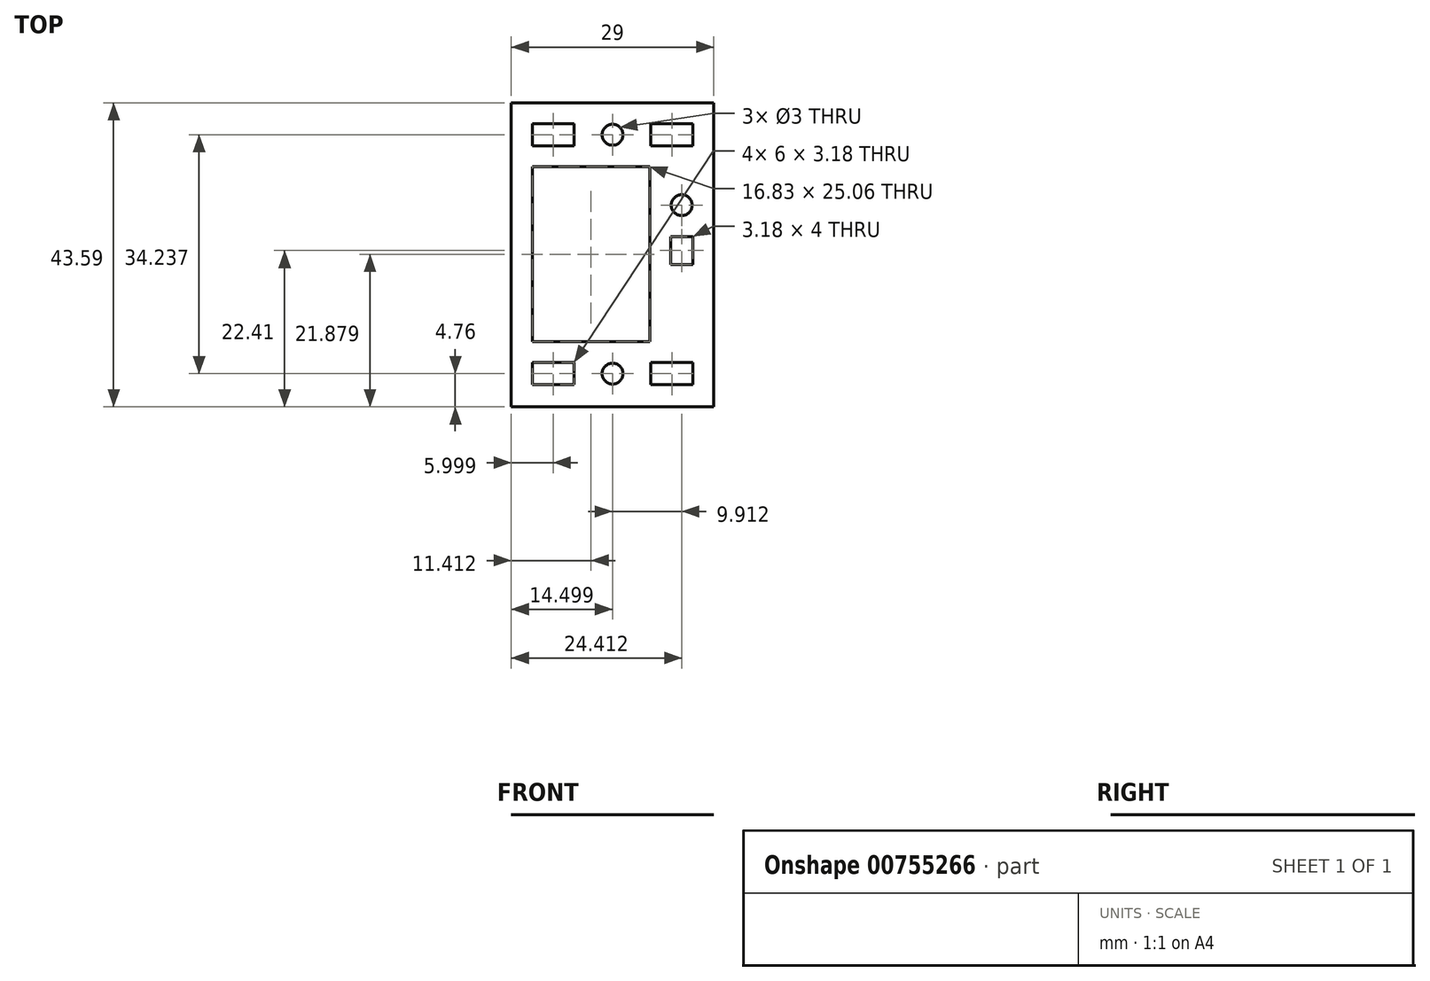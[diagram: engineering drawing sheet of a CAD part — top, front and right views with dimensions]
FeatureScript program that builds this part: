
annotation { "Feature Type Name" : "Feature", "Feature Type Description" : "" }
export const myFeature = defineFeature(function(context is Context, id is Id, definition is map)
    precondition{}
    {
        {
            var Q0;
            Q0=qCreatedBy(makeId("Top.planeOp"),FACE);
            var sketch = newSketch(context, id + "F0", { "sketchPlane" : qUnion([Q0])});
            skCircle(sketch, "E0", {"center": v(-29.12, -7.63) * mm, "radius": 1.5 * mm});
            skLineSegment(sketch, "E1.bottom", {"start": v(-23.62, -6.04) * mm, "end": v(-17.62, -6.04) * mm});
            skLineSegment(sketch, "E1.top", {"start": v(-23.62, -9.22) * mm, "end": v(-17.62, -9.22) * mm});
            skLineSegment(sketch, "E1.left", {"start": v(-23.62, -6.04) * mm, "end": v(-23.62, -9.22) * mm});
            skLineSegment(sketch, "E1.right", {"start": v(-17.62, -6.04) * mm, "end": v(-17.62, -9.22) * mm});
            skPoint(sketch, "E1.middle", {"position": v(-20.62, -7.63) * mm});
            skLineSegment(sketch, "E2.MirrorCS", {"start": v(-34.62, -6.04) * mm, "end": v(-40.62, -6.04) * mm});
            skLineSegment(sketch, "E3.MirrorCS", {"start": v(-34.62, -6.04) * mm, "end": v(-34.62, -9.22) * mm});
            skLineSegment(sketch, "E4.MirrorCS", {"start": v(-34.62, -9.22) * mm, "end": v(-40.62, -9.22) * mm});
            skLineSegment(sketch, "E5.MirrorCS", {"start": v(-40.62, -6.04) * mm, "end": v(-40.62, -9.22) * mm});
            skCircle(sketch, "E6", {"center": v(-29.12, 26.6) * mm, "radius": 1.5 * mm});
            skLineSegment(sketch, "E7.bottom", {"start": v(-23.62, 28.2) * mm, "end": v(-17.62, 28.2) * mm});
            skLineSegment(sketch, "E7.top", {"start": v(-23.62, 25.02) * mm, "end": v(-17.62, 25.02) * mm});
            skLineSegment(sketch, "E7.left", {"start": v(-23.62, 28.2) * mm, "end": v(-23.62, 25.02) * mm});
            skLineSegment(sketch, "E7.right", {"start": v(-17.62, 28.2) * mm, "end": v(-17.62, 25.02) * mm});
            skPoint(sketch, "E7.middle", {"position": v(-20.62, 26.6) * mm});
            skLineSegment(sketch, "E8.MirrorCS", {"start": v(-34.62, 28.2) * mm, "end": v(-34.62, 25.02) * mm});
            skLineSegment(sketch, "E9.MirrorCS", {"start": v(-34.62, 28.2) * mm, "end": v(-40.62, 28.2) * mm});
            skLineSegment(sketch, "E10.MirrorCS", {"start": v(-40.62, 28.2) * mm, "end": v(-40.62, 25.02) * mm});
            skLineSegment(sketch, "E11.MirrorCS", {"start": v(-34.62, 25.02) * mm, "end": v(-40.62, 25.02) * mm});
            skLineSegment(sketch, "E12", {"start": v(-43.62, -12.4) * mm, "end": v(-14.62, -12.4) * mm});
            skLineSegment(sketch, "E13", {"start": v(-43.62, -12.4) * mm, "end": v(-43.62, 31.2) * mm});
            skLineSegment(sketch, "E14", {"start": v(-14.62, -12.4) * mm, "end": v(-14.62, 31.2) * mm});
            skLineSegment(sketch, "E15", {"start": v(-14.62, 31.2) * mm, "end": v(-43.62, 31.2) * mm});
            skCircle(sketch, "E16", {"center": v(-19.2, 16.52) * mm, "radius": 1.5 * mm});
            skLineSegment(sketch, "E17.bottom", {"start": v(-20.8, 12.02) * mm, "end": v(-17.62, 12.02) * mm});
            skLineSegment(sketch, "E17.top", {"start": v(-20.8, 8.02) * mm, "end": v(-17.62, 8.02) * mm});
            skLineSegment(sketch, "E17.left", {"start": v(-20.8, 12.02) * mm, "end": v(-20.8, 8.02) * mm});
            skLineSegment(sketch, "E17.right", {"start": v(-17.62, 12.02) * mm, "end": v(-17.62, 8.02) * mm});
            skPoint(sketch, "E17.middle", {"position": v(-19.2, 10.02) * mm});
            skLineSegment(sketch, "E18.bottom", {"start": v(-40.62, 22.02) * mm, "end": v(-23.8, 22.02) * mm});
            skLineSegment(sketch, "E18.top", {"start": v(-40.62, -3.04) * mm, "end": v(-23.8, -3.04) * mm});
            skLineSegment(sketch, "E18.left", {"start": v(-40.62, 22.02) * mm, "end": v(-40.62, -3.04) * mm});
            skLineSegment(sketch, "E18.right", {"start": v(-23.8, 22.02) * mm, "end": v(-23.8, -3.04) * mm});
            skSolve(sketch);
        }
        {
            var Q0;
            Q0=makeQuery(id+"F0.imprint","IMPRINT",FACE,{"disambiguationData":[TD([[makeQuery(id+"F0.imprint","IMPRINT",EDGE,{"derivedFrom":sQuery(id+"F0.wireOp",EDGE,"E0")}),-1.0]])]});
            extrude(context, id + "F1", {"entities" : qUnion([Q0]), "depth" : 1 / 203.2 * mm, "offsetDistance" : 25 * mm});
        }
    });
